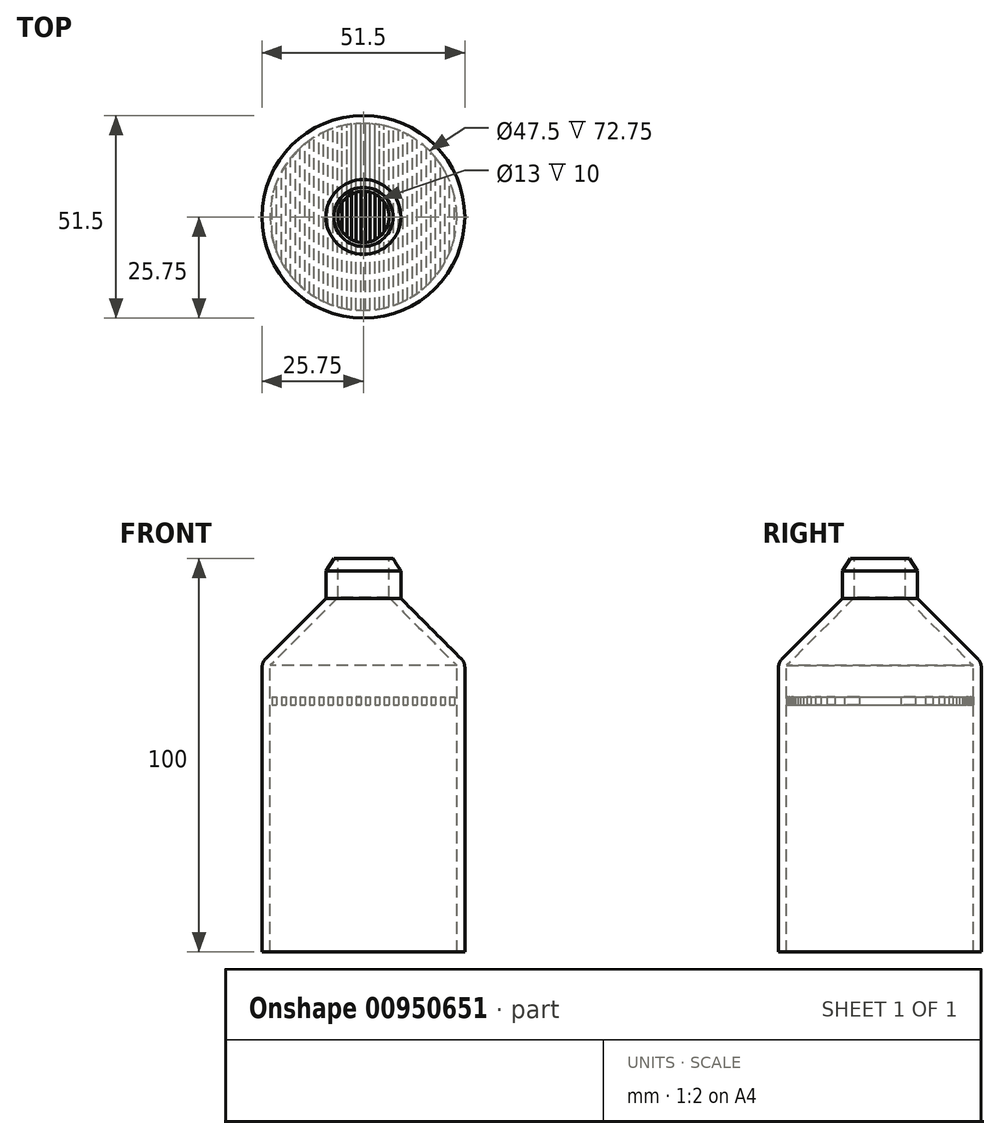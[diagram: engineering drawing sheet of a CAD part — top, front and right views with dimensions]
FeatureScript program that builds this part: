
annotation { "Feature Type Name" : "Feature", "Feature Type Description" : "" }
export const myFeature = defineFeature(function(context is Context, id is Id, definition is map)
    precondition{}
    {
        {
            var Q0;
            Q0=qCreatedBy(makeId("Front.planeOp"),FACE);
            var sketch = newSketch(context, id + "F0", { "sketchPlane" : qUnion([Q0])});
            skLineSegment(sketch, "E0", {"start": v(-7.5, 71.2) * mm, "end": v(-9.5, 68.03) * mm});
            skLineSegment(sketch, "E1", {"start": v(-9.5, 68.03) * mm, "end": v(-9.5, 61.03) * mm});
            skLineSegment(sketch, "E2", {"start": v(-9.5, 61.03) * mm, "end": v(-24.87, 45.66) * mm});
            skLineSegment(sketch, "E3", {"start": v(-7.5, 71.2) * mm, "end": v(-6.5, 71.2) * mm});
            skLineSegment(sketch, "E4", {"start": v(-6.5, 71.2) * mm, "end": v(-6.5, 61.2) * mm});
            skLineSegment(sketch, "E5", {"start": v(-6.5, 61.2) * mm, "end": v(-23.75, 43.95) * mm});
            skLineSegment(sketch, "E6", {"start": v(-23.75, 43.95) * mm, "end": v(-23.75, -28.8) * mm});
            skLineSegment(sketch, "E7", {"start": v(-25.75, 43.54) * mm, "end": v(-25.75, -28.8) * mm});
            skLineSegment(sketch, "E8", {"start": v(-25.75, -28.8) * mm, "end": v(-23.75, -28.8) * mm});
            skPoint(sketch, "E9.visualSharp", {"position": v(-25.75, 44.78) * mm});
            skArc(sketch, "E9.filletArc", {"start": v(-24.87, 45.66) * mm, "mid": v(-25.52, 44.68) * mm, "end": v(-25.75, 43.54) * mm});
            skSolve(sketch);
        }
        {
            var Q0;
            Q0=qCreatedBy(makeId("Front.planeOp"),FACE);
            var sketch = newSketch(context, id + "F1", { "sketchPlane" : qUnion([Q0])});
            skLineSegment(sketch, "E10", {"start": v(0, 66.56) * mm, "end": v(0, -48.76) * mm});
            skSolve(sketch);
        }
        {
            var Q0;
            Q0 = qSketchRegion(id + "F0", true);
            var Q1;
            Q1=sQuery(id+"F1.wireOp",EDGE,"E10");
            revolve(context, id + "F2", {"surfaceOperationType" : NewSurfaceOperationType.NEW, "entities" : qUnion([Q0]), "axis" : qUnion([Q1]), "revolveType" : RevolveType.FULL});
        }
        {
            var Q0;
            Q0=qCreatedBy(makeId("Top.planeOp"),FACE);
            var sketch = newSketch(context, id + "F3", { "sketchPlane" : qUnion([Q0])});
            skLineSegment(sketch, "E11.left", {"start": v(-23.2, -5.26) * mm, "end": v(-23.2, 5.3) * mm});
            skLineSegment(sketch, "E11.right", {"start": v(-22.02, -9.01) * mm, "end": v(-22.02, 9.04) * mm});
            skLineSegment(sketch, "E12.1.0.0", {"start": v(-19.64, -13.4) * mm, "end": v(-19.64, 13.44) * mm});
            skLineSegment(sketch, "E12.1.0.1", {"start": v(-20.83, -11.48) * mm, "end": v(-20.83, 11.51) * mm});
            skLineSegment(sketch, "E12.2.0.0", {"start": v(-17.27, -16.34) * mm, "end": v(-17.27, 16.37) * mm});
            skLineSegment(sketch, "E12.2.0.1", {"start": v(-18.45, -15) * mm, "end": v(-18.45, 15.02) * mm});
            skLineSegment(sketch, "E12.3.0.0", {"start": v(-14.9, -18.53) * mm, "end": v(-14.9, 18.55) * mm});
            skLineSegment(sketch, "E12.3.0.1", {"start": v(-16.08, -17.5) * mm, "end": v(-16.08, 17.54) * mm});
            skLineSegment(sketch, "E12.4.0.0", {"start": v(-12.52, -20.2) * mm, "end": v(-12.52, 20.23) * mm});
            skLineSegment(sketch, "E12.4.0.1", {"start": v(-13.7, -19.42) * mm, "end": v(-13.7, 19.44) * mm});
            skLineSegment(sketch, "E12.5.0.0", {"start": v(-10.14, -21.48) * mm, "end": v(-10.14, 21.51) * mm});
            skLineSegment(sketch, "E12.5.0.1", {"start": v(-11.33, -20.89) * mm, "end": v(-11.33, 20.91) * mm});
            skLineSegment(sketch, "E12.6.0.0", {"start": v(-7.77, -22.45) * mm, "end": v(-7.77, 22.47) * mm});
            skLineSegment(sketch, "E12.6.0.1", {"start": v(-8.95, -22) * mm, "end": v(-8.95, 22.03) * mm});
            skLineSegment(sketch, "E12.7.0.0", {"start": v(-5.4, -23.13) * mm, "end": v(-5.4, 23.15) * mm});
            skLineSegment(sketch, "E12.7.0.1", {"start": v(-6.58, -22.82) * mm, "end": v(-6.58, 22.85) * mm});
            skLineSegment(sketch, "E12.8.0.0", {"start": v(-3.02, -23.55) * mm, "end": v(-3.02, 23.58) * mm});
            skLineSegment(sketch, "E12.8.0.1", {"start": v(-4.2, -23.37) * mm, "end": v(-4.2, 23.4) * mm});
            skLineSegment(sketch, "E12.9.0.0", {"start": v(-0.64, -23.73) * mm, "end": v(-0.64, 23.76) * mm});
            skLineSegment(sketch, "E12.9.0.1", {"start": v(-1.83, -23.67) * mm, "end": v(-1.83, 23.7) * mm});
            skLineSegment(sketch, "E12.10.0.0", {"start": v(1.73, -23.67) * mm, "end": v(1.73, 23.7) * mm});
            skLineSegment(sketch, "E12.10.0.1", {"start": v(0.55, -23.73) * mm, "end": v(0.55, 23.76) * mm});
            skLineSegment(sketch, "E12.11.0.0", {"start": v(4.1, -23.37) * mm, "end": v(4.1, 23.4) * mm});
            skLineSegment(sketch, "E12.11.0.1", {"start": v(2.92, -23.55) * mm, "end": v(2.92, 23.58) * mm});
            skLineSegment(sketch, "E12.12.0.0", {"start": v(6.48, -22.82) * mm, "end": v(6.48, 22.85) * mm});
            skLineSegment(sketch, "E12.12.0.1", {"start": v(5.3, -23.13) * mm, "end": v(5.3, 23.15) * mm});
            skLineSegment(sketch, "E12.13.0.0", {"start": v(8.86, -22) * mm, "end": v(8.86, 22.03) * mm});
            skLineSegment(sketch, "E12.13.0.1", {"start": v(7.67, -22.45) * mm, "end": v(7.67, 22.47) * mm});
            skLineSegment(sketch, "E12.14.0.0", {"start": v(11.23, -20.89) * mm, "end": v(11.23, 20.91) * mm});
            skLineSegment(sketch, "E12.14.0.1", {"start": v(10.05, -21.48) * mm, "end": v(10.05, 21.51) * mm});
            skLineSegment(sketch, "E12.15.0.0", {"start": v(13.6, -19.42) * mm, "end": v(13.6, 19.44) * mm});
            skLineSegment(sketch, "E12.15.0.1", {"start": v(12.42, -20.2) * mm, "end": v(12.42, 20.23) * mm});
            skLineSegment(sketch, "E12.16.0.0", {"start": v(15.98, -17.5) * mm, "end": v(15.98, 17.54) * mm});
            skLineSegment(sketch, "E12.16.0.1", {"start": v(14.8, -18.53) * mm, "end": v(14.8, 18.55) * mm});
            skLineSegment(sketch, "E12.17.0.0", {"start": v(18.36, -15) * mm, "end": v(18.36, 15.02) * mm});
            skLineSegment(sketch, "E12.17.0.1", {"start": v(17.17, -16.34) * mm, "end": v(17.17, 16.37) * mm});
            skLineSegment(sketch, "E12.18.0.0", {"start": v(20.73, -11.48) * mm, "end": v(20.73, 11.51) * mm});
            skLineSegment(sketch, "E12.18.0.1", {"start": v(19.55, -13.4) * mm, "end": v(19.55, 13.44) * mm});
            skLineSegment(sketch, "E12.19.0.0", {"start": v(23.1, -5.26) * mm, "end": v(23.1, 5.3) * mm});
            skLineSegment(sketch, "E12.19.0.1", {"start": v(21.92, -9.01) * mm, "end": v(21.92, 9.04) * mm});
            skArc(sketch, "E13", {"start": v(-23.2, -5.26) * mm, "mid": v(-22.69, -7.16) * mm, "end": v(-22.02, -9.01) * mm});
            skArc(sketch, "E14.trimOffspring", {"start": v(-20.83, -11.48) * mm, "mid": v(-20.26, -12.46) * mm, "end": v(-19.64, -13.4) * mm});
            skArc(sketch, "E15.trimOffspring", {"start": v(-18.45, -15) * mm, "mid": v(-17.87, -15.68) * mm, "end": v(-17.27, -16.34) * mm});
            skArc(sketch, "E16.trimOffspring", {"start": v(-16.08, -17.5) * mm, "mid": v(-15.5, -18.03) * mm, "end": v(-14.9, -18.53) * mm});
            skArc(sketch, "E17.trimOffspring", {"start": v(-13.7, -19.42) * mm, "mid": v(-13.12, -19.82) * mm, "end": v(-12.52, -20.2) * mm});
            skArc(sketch, "E18.trimOffspring", {"start": v(-11.33, -20.89) * mm, "mid": v(-10.74, -21.2) * mm, "end": v(-10.14, -21.48) * mm});
            skArc(sketch, "E19.trimOffspring", {"start": v(-8.95, -22) * mm, "mid": v(-8.36, -22.23) * mm, "end": v(-7.77, -22.45) * mm});
            skArc(sketch, "E20.trimOffspring", {"start": v(-6.58, -22.82) * mm, "mid": v(-5.99, -22.98) * mm, "end": v(-5.4, -23.13) * mm});
            skArc(sketch, "E21.trimOffspring", {"start": v(-4.2, -23.37) * mm, "mid": v(-3.61, -23.47) * mm, "end": v(-3.02, -23.55) * mm});
            skArc(sketch, "E22.trimOffspring", {"start": v(-1.83, -23.67) * mm, "mid": v(-1.24, -23.7) * mm, "end": v(-0.64, -23.73) * mm});
            skArc(sketch, "E23.trimOffspring", {"start": v(0.55, -23.73) * mm, "mid": v(1.14, -23.7) * mm, "end": v(1.73, -23.67) * mm});
            skArc(sketch, "E24.trimOffspring", {"start": v(2.92, -23.55) * mm, "mid": v(3.52, -23.47) * mm, "end": v(4.1, -23.37) * mm});
            skArc(sketch, "E25.trimOffspring", {"start": v(5.3, -23.13) * mm, "mid": v(5.9, -22.98) * mm, "end": v(6.48, -22.82) * mm});
            skArc(sketch, "E26.trimOffspring", {"start": v(7.67, -22.45) * mm, "mid": v(8.27, -22.23) * mm, "end": v(8.86, -22) * mm});
            skArc(sketch, "E27.trimOffspring", {"start": v(10.05, -21.48) * mm, "mid": v(10.64, -21.2) * mm, "end": v(11.23, -20.89) * mm});
            skArc(sketch, "E28.trimOffspring", {"start": v(12.42, -20.2) * mm, "mid": v(13.02, -19.82) * mm, "end": v(13.6, -19.42) * mm});
            skArc(sketch, "E29.trimOffspring", {"start": v(14.8, -18.53) * mm, "mid": v(15.4, -18.03) * mm, "end": v(15.98, -17.5) * mm});
            skArc(sketch, "E30.trimOffspring", {"start": v(17.17, -16.34) * mm, "mid": v(17.78, -15.68) * mm, "end": v(18.36, -15) * mm});
            skArc(sketch, "E31.trimOffspring", {"start": v(19.55, -13.4) * mm, "mid": v(20.16, -12.46) * mm, "end": v(20.73, -11.48) * mm});
            skArc(sketch, "E32.trimOffspring", {"start": v(21.92, -9.01) * mm, "mid": v(22.6, -7.16) * mm, "end": v(23.1, -5.26) * mm});
            skArc(sketch, "E33.trimOffspring", {"start": v(23.1, 5.3) * mm, "mid": v(22.6, 7.19) * mm, "end": v(21.92, 9.04) * mm});
            skArc(sketch, "E34.trimOffspring", {"start": v(20.73, 11.51) * mm, "mid": v(20.16, 12.49) * mm, "end": v(19.55, 13.44) * mm});
            skArc(sketch, "E35.trimOffspring", {"start": v(18.36, 15.02) * mm, "mid": v(17.78, 15.7) * mm, "end": v(17.17, 16.37) * mm});
            skArc(sketch, "E36.trimOffspring", {"start": v(15.98, 17.54) * mm, "mid": v(15.4, 18.06) * mm, "end": v(14.8, 18.55) * mm});
            skArc(sketch, "E37.trimOffspring", {"start": v(13.6, 19.44) * mm, "mid": v(13.02, 19.85) * mm, "end": v(12.42, 20.23) * mm});
            skArc(sketch, "E38.trimOffspring", {"start": v(11.23, 20.91) * mm, "mid": v(10.64, 21.22) * mm, "end": v(10.05, 21.51) * mm});
            skArc(sketch, "E39.trimOffspring", {"start": v(8.86, 22.03) * mm, "mid": v(8.27, 22.26) * mm, "end": v(7.67, 22.47) * mm});
            skArc(sketch, "E40.trimOffspring", {"start": v(6.48, 22.85) * mm, "mid": v(5.9, 23) * mm, "end": v(5.3, 23.15) * mm});
            skArc(sketch, "E41.trimOffspring", {"start": v(4.1, 23.4) * mm, "mid": v(3.52, 23.5) * mm, "end": v(2.92, 23.58) * mm});
            skArc(sketch, "E42.trimOffspring", {"start": v(1.73, 23.7) * mm, "mid": v(1.14, 23.73) * mm, "end": v(0.55, 23.76) * mm});
            skArc(sketch, "E43.trimOffspring", {"start": v(-0.64, 23.76) * mm, "mid": v(-1.24, 23.73) * mm, "end": v(-1.83, 23.7) * mm});
            skArc(sketch, "E44.trimOffspring", {"start": v(-3.02, 23.58) * mm, "mid": v(-3.61, 23.5) * mm, "end": v(-4.2, 23.4) * mm});
            skArc(sketch, "E45.trimOffspring", {"start": v(-5.4, 23.15) * mm, "mid": v(-5.99, 23) * mm, "end": v(-6.58, 22.85) * mm});
            skArc(sketch, "E46.trimOffspring", {"start": v(-7.77, 22.47) * mm, "mid": v(-8.36, 22.26) * mm, "end": v(-8.95, 22.03) * mm});
            skArc(sketch, "E47.trimOffspring", {"start": v(-10.14, 21.51) * mm, "mid": v(-10.74, 21.22) * mm, "end": v(-11.33, 20.91) * mm});
            skArc(sketch, "E48.trimOffspring", {"start": v(-12.52, 20.23) * mm, "mid": v(-13.12, 19.85) * mm, "end": v(-13.7, 19.44) * mm});
            skArc(sketch, "E49.trimOffspring", {"start": v(-14.9, 18.55) * mm, "mid": v(-15.5, 18.06) * mm, "end": v(-16.08, 17.54) * mm});
            skArc(sketch, "E50.trimOffspring", {"start": v(-17.27, 16.37) * mm, "mid": v(-17.87, 15.7) * mm, "end": v(-18.45, 15.02) * mm});
            skArc(sketch, "E51.trimOffspring", {"start": v(-19.64, 13.44) * mm, "mid": v(-20.26, 12.49) * mm, "end": v(-20.83, 11.51) * mm});
            skArc(sketch, "E52.trimOffspring", {"start": v(-22.02, 9.04) * mm, "mid": v(-22.69, 7.19) * mm, "end": v(-23.2, 5.3) * mm});
            skSolve(sketch);
        }
        {
            var Q0;
            Q0 = qSketchRegion(id + "F3", true);
            extrude(context, id + "F4", {"entities" : qUnion([Q0]), "depth" : 2 * mm, "offsetDistance" : 25 * mm});
        }
        {
            var Q0;
            Q0=makeQuery(id+"F4.opExtrude","SWEPT_BODY",BODY,{"disambiguationData":[OSD([sQuery(id+"F3.wireOp",EDGE,"E12.1.0.0"),sQuery(id+"F3.wireOp",EDGE,"E12.1.0.1"),sQuery(id+"F3.wireOp",EDGE,"E14.trimOffspring"),sQuery(id+"F3.wireOp",EDGE,"E51.trimOffspring")])]});
            var Q1;
            Q1=makeQuery(id+"F4.opExtrude","SWEPT_BODY",BODY,{"disambiguationData":[OSD([sQuery(id+"F3.wireOp",EDGE,"E12.2.0.0"),sQuery(id+"F3.wireOp",EDGE,"E12.2.0.1"),sQuery(id+"F3.wireOp",EDGE,"E15.trimOffspring"),sQuery(id+"F3.wireOp",EDGE,"E50.trimOffspring")])]});
            var Q2;
            Q2=makeQuery(id+"F4.opExtrude","SWEPT_BODY",BODY,{"disambiguationData":[OSD([sQuery(id+"F3.wireOp",EDGE,"E12.3.0.0"),sQuery(id+"F3.wireOp",EDGE,"E12.3.0.1"),sQuery(id+"F3.wireOp",EDGE,"E16.trimOffspring"),sQuery(id+"F3.wireOp",EDGE,"E49.trimOffspring")])]});
            var Q3;
            Q3=makeQuery(id+"F4.opExtrude","SWEPT_BODY",BODY,{"disambiguationData":[OSD([sQuery(id+"F3.wireOp",EDGE,"E12.4.0.0"),sQuery(id+"F3.wireOp",EDGE,"E12.4.0.1"),sQuery(id+"F3.wireOp",EDGE,"E17.trimOffspring"),sQuery(id+"F3.wireOp",EDGE,"E48.trimOffspring")])]});
            var Q4;
            Q4=makeQuery(id+"F4.opExtrude","SWEPT_BODY",BODY,{"disambiguationData":[OSD([sQuery(id+"F3.wireOp",EDGE,"E12.5.0.0"),sQuery(id+"F3.wireOp",EDGE,"E12.5.0.1"),sQuery(id+"F3.wireOp",EDGE,"E18.trimOffspring"),sQuery(id+"F3.wireOp",EDGE,"E47.trimOffspring")])]});
            var Q5;
            Q5=makeQuery(id+"F4.opExtrude","SWEPT_BODY",BODY,{"disambiguationData":[OSD([sQuery(id+"F3.wireOp",EDGE,"E12.6.0.0"),sQuery(id+"F3.wireOp",EDGE,"E12.6.0.1"),sQuery(id+"F3.wireOp",EDGE,"E19.trimOffspring"),sQuery(id+"F3.wireOp",EDGE,"E46.trimOffspring")])]});
            var Q6;
            Q6=makeQuery(id+"F4.opExtrude","SWEPT_BODY",BODY,{"disambiguationData":[OSD([sQuery(id+"F3.wireOp",EDGE,"E12.7.0.0"),sQuery(id+"F3.wireOp",EDGE,"E12.7.0.1"),sQuery(id+"F3.wireOp",EDGE,"E20.trimOffspring"),sQuery(id+"F3.wireOp",EDGE,"E45.trimOffspring")])]});
            var Q7;
            Q7=makeQuery(id+"F4.opExtrude","SWEPT_BODY",BODY,{"disambiguationData":[OSD([sQuery(id+"F3.wireOp",EDGE,"E12.8.0.0"),sQuery(id+"F3.wireOp",EDGE,"E12.8.0.1"),sQuery(id+"F3.wireOp",EDGE,"E21.trimOffspring"),sQuery(id+"F3.wireOp",EDGE,"E44.trimOffspring")])]});
            var Q8;
            Q8=makeQuery(id+"F4.opExtrude","SWEPT_BODY",BODY,{"disambiguationData":[OSD([sQuery(id+"F3.wireOp",EDGE,"E12.9.0.0"),sQuery(id+"F3.wireOp",EDGE,"E12.9.0.1"),sQuery(id+"F3.wireOp",EDGE,"E22.trimOffspring"),sQuery(id+"F3.wireOp",EDGE,"E43.trimOffspring")])]});
            var Q9;
            Q9=makeQuery(id+"F4.opExtrude","SWEPT_BODY",BODY,{"disambiguationData":[OSD([sQuery(id+"F3.wireOp",EDGE,"E12.10.0.0"),sQuery(id+"F3.wireOp",EDGE,"E12.10.0.1"),sQuery(id+"F3.wireOp",EDGE,"E23.trimOffspring"),sQuery(id+"F3.wireOp",EDGE,"E42.trimOffspring")])]});
            var Q10;
            Q10=makeQuery(id+"F4.opExtrude","SWEPT_BODY",BODY,{"disambiguationData":[OSD([sQuery(id+"F3.wireOp",EDGE,"E12.11.0.0"),sQuery(id+"F3.wireOp",EDGE,"E12.11.0.1"),sQuery(id+"F3.wireOp",EDGE,"E24.trimOffspring"),sQuery(id+"F3.wireOp",EDGE,"E41.trimOffspring")])]});
            var Q11;
            Q11=makeQuery(id+"F4.opExtrude","SWEPT_BODY",BODY,{"disambiguationData":[OSD([sQuery(id+"F3.wireOp",EDGE,"E12.12.0.0"),sQuery(id+"F3.wireOp",EDGE,"E12.12.0.1"),sQuery(id+"F3.wireOp",EDGE,"E25.trimOffspring"),sQuery(id+"F3.wireOp",EDGE,"E40.trimOffspring")])]});
            var Q12;
            Q12=makeQuery(id+"F4.opExtrude","SWEPT_BODY",BODY,{"disambiguationData":[OSD([sQuery(id+"F3.wireOp",EDGE,"E12.13.0.0"),sQuery(id+"F3.wireOp",EDGE,"E12.13.0.1"),sQuery(id+"F3.wireOp",EDGE,"E26.trimOffspring"),sQuery(id+"F3.wireOp",EDGE,"E39.trimOffspring")])]});
            var Q13;
            Q13=makeQuery(id+"F4.opExtrude","SWEPT_BODY",BODY,{"disambiguationData":[OSD([sQuery(id+"F3.wireOp",EDGE,"E12.14.0.0"),sQuery(id+"F3.wireOp",EDGE,"E12.14.0.1"),sQuery(id+"F3.wireOp",EDGE,"E27.trimOffspring"),sQuery(id+"F3.wireOp",EDGE,"E38.trimOffspring")])]});
            var Q14;
            Q14=makeQuery(id+"F4.opExtrude","SWEPT_BODY",BODY,{"disambiguationData":[OSD([sQuery(id+"F3.wireOp",EDGE,"E12.15.0.0"),sQuery(id+"F3.wireOp",EDGE,"E12.15.0.1"),sQuery(id+"F3.wireOp",EDGE,"E28.trimOffspring"),sQuery(id+"F3.wireOp",EDGE,"E37.trimOffspring")])]});
            var Q15;
            Q15=makeQuery(id+"F4.opExtrude","SWEPT_BODY",BODY,{"disambiguationData":[OSD([sQuery(id+"F3.wireOp",EDGE,"E12.16.0.0"),sQuery(id+"F3.wireOp",EDGE,"E12.16.0.1"),sQuery(id+"F3.wireOp",EDGE,"E29.trimOffspring"),sQuery(id+"F3.wireOp",EDGE,"E36.trimOffspring")])]});
            var Q16;
            Q16=makeQuery(id+"F4.opExtrude","SWEPT_BODY",BODY,{"disambiguationData":[OSD([sQuery(id+"F3.wireOp",EDGE,"E12.17.0.0"),sQuery(id+"F3.wireOp",EDGE,"E12.17.0.1"),sQuery(id+"F3.wireOp",EDGE,"E30.trimOffspring"),sQuery(id+"F3.wireOp",EDGE,"E35.trimOffspring")])]});
            var Q17;
            Q17=makeQuery(id+"F4.opExtrude","SWEPT_BODY",BODY,{"disambiguationData":[OSD([sQuery(id+"F3.wireOp",EDGE,"E12.18.0.0"),sQuery(id+"F3.wireOp",EDGE,"E12.18.0.1"),sQuery(id+"F3.wireOp",EDGE,"E31.trimOffspring"),sQuery(id+"F3.wireOp",EDGE,"E34.trimOffspring")])]});
            var Q18;
            Q18=makeQuery(id+"F4.opExtrude","SWEPT_BODY",BODY,{"disambiguationData":[OSD([sQuery(id+"F3.wireOp",EDGE,"E12.19.0.0"),sQuery(id+"F3.wireOp",EDGE,"E12.19.0.1"),sQuery(id+"F3.wireOp",EDGE,"E32.trimOffspring"),sQuery(id+"F3.wireOp",EDGE,"E33.trimOffspring")])]});
            var Q19;
            Q19=makeQuery(id+"F4.opExtrude","SWEPT_BODY",BODY,{"disambiguationData":[OSD([sQuery(id+"F3.wireOp",EDGE,"E11.left"),sQuery(id+"F3.wireOp",EDGE,"E11.right"),sQuery(id+"F3.wireOp",EDGE,"E13"),sQuery(id+"F3.wireOp",EDGE,"E52.trimOffspring")])]});
            transform(context, id + "F5", {"entities" : qUnion([Q0, Q1, Q2, Q3, Q4, Q5, Q6, Q7, Q8, Q9, Q10, Q11, Q12, Q13, Q14, Q15, Q16, Q17, Q18, Q19]), "transformType" : TransformType.TRANSLATION_3D, "dx" : 0 * mm, "dy" : 0 * mm, "dz" : 34 * mm, "makeCopy" : false});
        }
    });
